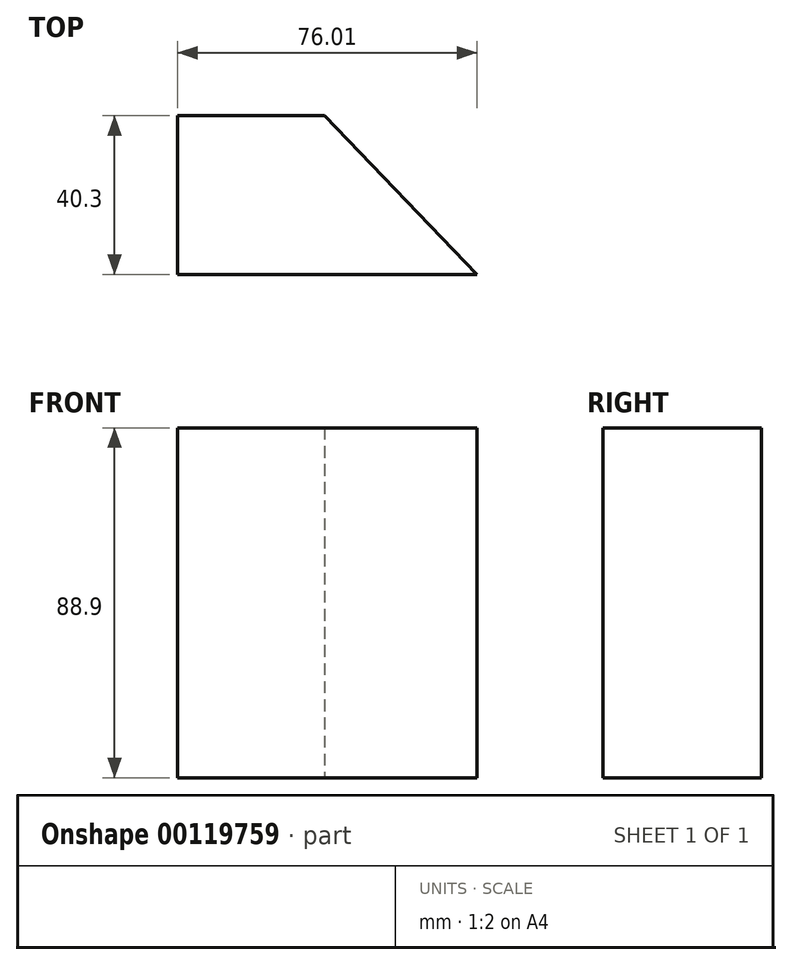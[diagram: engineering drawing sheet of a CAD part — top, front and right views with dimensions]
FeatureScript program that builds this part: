
annotation { "Feature Type Name" : "Feature", "Feature Type Description" : "" }
export const myFeature = defineFeature(function(context is Context, id is Id, definition is map)
    precondition{}
    {
        {
            var Q0;
            Q0=qCreatedBy(makeId("Top.planeOp"),FACE);
            var sketch = newSketch(context, id + "F0", { "sketchPlane" : qUnion([Q0])});
            skLineSegment(sketch, "E0", {"start": v(0, 0) * mm, "end": v(0, 40.3) * mm});
            skLineSegment(sketch, "E1", {"start": v(0, 40.3) * mm, "end": v(37.34, 40.3) * mm});
            skLineSegment(sketch, "E2", {"start": v(37.34, 40.3) * mm, "end": v(76, 0) * mm});
            skLineSegment(sketch, "E3", {"start": v(76, 0) * mm, "end": v(0, 0) * mm});
            skSolve(sketch);
        }
        {
            var Q0;
            Q0 = qSketchRegion(id + "F0", true);
            extrude(context, id + "F1", {"entities" : qUnion([Q0]), "depth" : 88.9 * mm});
        }
    });
